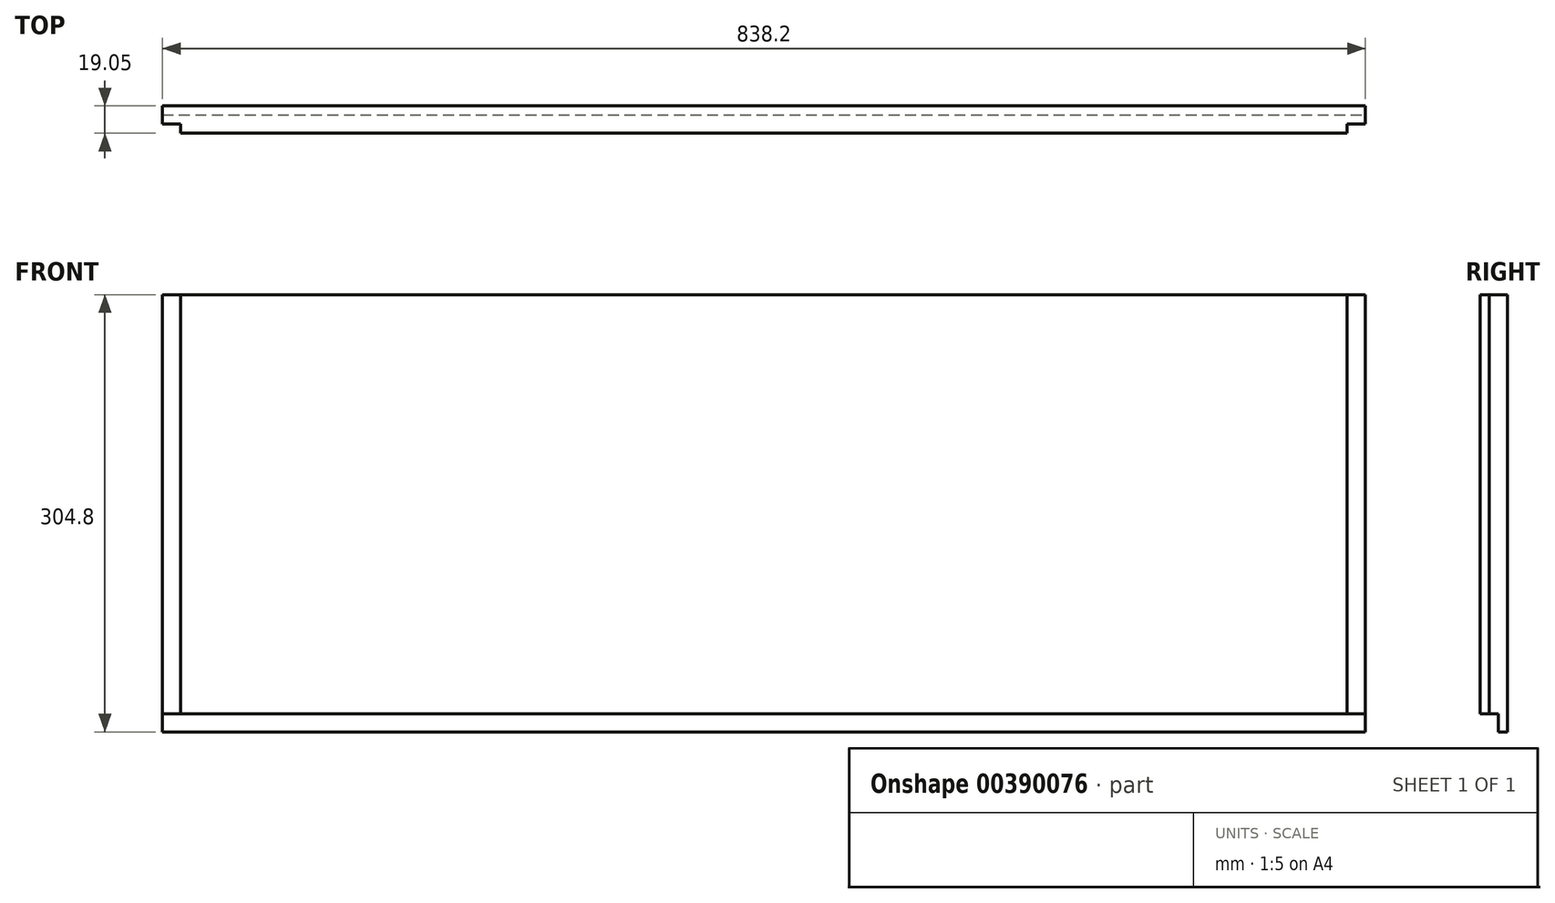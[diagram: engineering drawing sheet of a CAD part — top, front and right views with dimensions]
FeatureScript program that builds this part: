
annotation { "Feature Type Name" : "Feature", "Feature Type Description" : "" }
export const myFeature = defineFeature(function(context is Context, id is Id, definition is map)
    precondition{}
    {
        {
            var Q0;
            Q0=qCreatedBy(makeId("Front.planeOp"),FACE);
            var sketch = newSketch(context, id + "F0", { "sketchPlane" : qUnion([Q0])});
            skLineSegment(sketch, "E0.bottom", {"start": v(0, 0) * mm, "end": v(838.2, 0) * mm});
            skLineSegment(sketch, "E0.top", {"start": v(0, 304.8) * mm, "end": v(838.2, 304.8) * mm});
            skLineSegment(sketch, "E0.left", {"start": v(0, 0) * mm, "end": v(0, 304.8) * mm});
            skLineSegment(sketch, "E0.right", {"start": v(838.2, 0) * mm, "end": v(838.2, 304.8) * mm});
            skSolve(sketch);
        }
        {
            var Q0;
            Q0=makeQuery(id+"F0.imprint","IMPRINT",FACE,{"disambiguationData":[TD([[makeQuery(id+"F0.imprint","IMPRINT",EDGE,{"derivedFrom":sQuery(id+"F0.wireOp",EDGE,"E0.bottom")}),1.0]])]});
            extrude(context, id + "F1", {"entities" : qUnion([Q0]), "depth" : 19.05 * mm});
        }
        {
            var Q0;
            Q0=makeQuery(id+"F1.opExtrude","SWEPT_FACE",FACE,{"disambiguationData":[OSD([sQuery(id+"F0.wireOp",EDGE,"E0.right")])]});
            var sketch = newSketch(context, id + "F2", { "sketchPlane" : qUnion([Q0])});
            skLineSegment(sketch, "E1.bottom", {"start": v(-19.05, 0) * mm, "end": v(-6.35, 0) * mm});
            skLineSegment(sketch, "E1.top", {"start": v(-19.05, 12.7) * mm, "end": v(-6.35, 12.7) * mm});
            skLineSegment(sketch, "E1.left", {"start": v(-19.05, 0) * mm, "end": v(-19.05, 12.7) * mm});
            skLineSegment(sketch, "E1.right", {"start": v(-6.35, 0) * mm, "end": v(-6.35, 12.7) * mm});
            skSolve(sketch);
        }
        {
            var Q0;
            Q0 = qSketchRegion(id + "F2", true);
            extrude(context, id + "F3", {"entities" : qUnion([Q0]), "operationType" : NewBodyOperationType.REMOVE, "endBound" : BoundingType.THROUGH_ALL, "oppositeDirection" : true, "depth" : 25.4 * mm});
        }
        {
            var Q0;
            Q0=makeQuery(id+"F1.opExtrude","SWEPT_FACE",FACE,{"disambiguationData":[OSD([sQuery(id+"F0.wireOp",EDGE,"E0.top")])]});
            var sketch = newSketch(context, id + "F4", { "sketchPlane" : qUnion([Q0])});
            skLineSegment(sketch, "E2.bottom", {"start": v(0, -19.05) * mm, "end": v(12.7, -19.05) * mm});
            skLineSegment(sketch, "E2.top", {"start": v(0, -12.7) * mm, "end": v(12.7, -12.7) * mm});
            skLineSegment(sketch, "E2.left", {"start": v(0, -19.05) * mm, "end": v(0, -12.7) * mm});
            skLineSegment(sketch, "E2.right", {"start": v(12.7, -19.05) * mm, "end": v(12.7, -12.7) * mm});
            skLineSegment(sketch, "E3.bottom", {"start": v(838.2, -19.05) * mm, "end": v(825.5, -19.05) * mm});
            skLineSegment(sketch, "E3.top", {"start": v(838.2, -12.7) * mm, "end": v(825.5, -12.7) * mm});
            skLineSegment(sketch, "E3.left", {"start": v(838.2, -19.05) * mm, "end": v(838.2, -12.7) * mm});
            skLineSegment(sketch, "E3.right", {"start": v(825.5, -19.05) * mm, "end": v(825.5, -12.7) * mm});
            skSolve(sketch);
        }
        {
            var Q0;
            Q0=makeQuery(id+"F4.imprint","IMPRINT",FACE,{"disambiguationData":[TD([[makeQuery(id+"F4.imprint","IMPRINT",EDGE,{"derivedFrom":sQuery(id+"F4.wireOp",EDGE,"E3.bottom")}),1.0]])]});
            var Q1;
            Q1=makeQuery(id+"F4.imprint","IMPRINT",FACE,{"disambiguationData":[TD([[makeQuery(id+"F4.imprint","IMPRINT",EDGE,{"derivedFrom":sQuery(id+"F4.wireOp",EDGE,"E2.bottom")}),1.0]])]});
            extrude(context, id + "F5", {"entities" : qUnion([Q0, Q1]), "operationType" : NewBodyOperationType.REMOVE, "endBound" : BoundingType.THROUGH_ALL, "oppositeDirection" : true, "depth" : 25.4 * mm});
        }
    });
